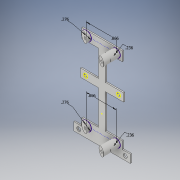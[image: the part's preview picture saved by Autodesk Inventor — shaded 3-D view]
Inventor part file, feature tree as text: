
AUTODESK INVENTOR PART (.ipt)
format: ipt  version: 2018 (Build 220112000, 112)  size: 297,472 bytes
history: native  units: in
note: dims shown in document units (in); Inventor stores cm internally (conversion verified against a paired STEP export)
features: extrude x11, sketch x8
ambient origin geometry x8: Origin, YZ Plane, XZ Plane, XY Plane, X Axis, Y Axis, Z Axis, Center Point
bodies: Solid1 (feature_tree)
feature tree (19):
  extrude  "Extrusion1"  Depth=1.2598in
  extrude  "Extrusion2"  TaperAngle=0.0deg  [1 undecoded]
  extrude  "Extrusion3"  Depth=0.2362in
  sketch  "Sketch5"  dims[d7=0.0in d8=0.0394in d9=0.0in]
  extrude  "Extrusion5"  Depth=0.0394in TaperAngle=0.0deg
  extrude  "Extrusion6"  Depth=0.6791in
  extrude  "Extrusion9"  Depth=0.1181in
  extrude  "Extrusion14"  Depth=0.9646in
  extrude  "Extrusion11"  Depth=0.0394in
  extrude  "Extrusion12"  Depth=0.0394in
  extrude  "Extrusion13"  Depth=0.0394in
  extrude  "Extrusion15"  Depth=0.0394in TaperAngle=0.0deg
  sketch  "Sketch1"  dims[d0=0.1969in d2=1.2598in]
  sketch  "Sketch2"  dims[d3=0.2362in d4=0.0in]
  sketch  "Sketch4"  dims[d5=1.6535in d6=0.2362in]
  sketch  "Sketch6"  dims[d10=1.3583in d13=0.6791in]
  sketch  "Sketch9"  dims[d14=0.6791in d15=0.1181in]
  sketch  "Sketch10"  dims[d16=0.1181in d17=0.9646in]
  sketch  "Sketch12"  dims[d18=0.4823in d19=0.4823in d20=0.1181in d21=0.1181in d22=0.0787in d23=0.0in d28=2.2835in d29=0.1969in d30=0.0in d31=0.0in d32=0.1969in d33=1.1811in d34=1.1811in d35=0.2756in d36=0.2756in d37=0.0787in d38=0.0787in d39=0.0787in d40=0.0787in d41=0.9055in d42=0.9055in d43=0.4528in d44=0.4528in d45=0.4528in d46=0.4528in d47=0.0394in d48=0.0in d52=0.2756in d55=0.2756in d57=0.0787in d58=0.0in d59=0.2362in d60=0.2362in d61=0.2362in d62=0.2362in d63=0.0787in d64=0.0in d65=1.4567in d66=1.4567in d72=0.4604in d73=0.25in d74=0.0in d77=3.0in d78=0.0in d79=0.0394in d80=0.0in d81=0.9055in d82=2.2835in d83=0.1293in d84=0.1293in d85=0.1893in d86=0.1893in d87=0.0787in d88=0.0787in d89=0.0787in d90=0.0787in d91=0.1181in d92=0.0in d97=0.2362in d98=0.8661in d99=0.2362in d100=0.8661in d101=0.4724in d102=0.0in d103=0.0787in d104=0.0787in d105=0.9075in d106=0.1969in d110=0.0787in d111=0.0787in d112=0.9075in d113=0.1969in d114=0.1969in d115=0.0in]
note: 1 required parameter value undecoded (feature->parameter linkage not recoverable at this tier; creation-order binding heuristic only, values carry confidence <= 0.55)
